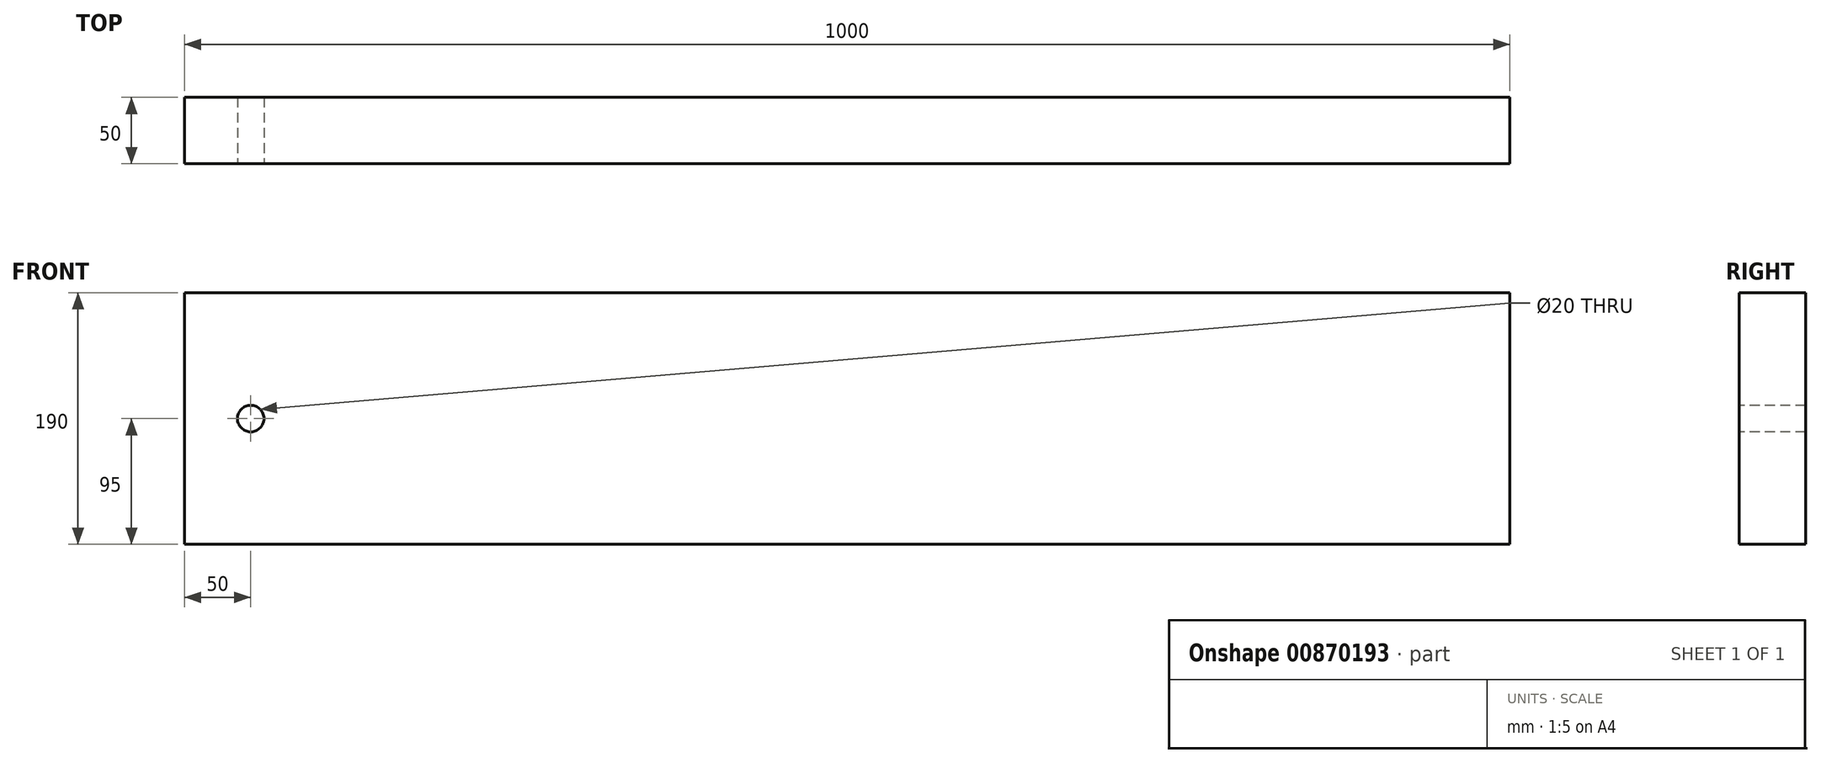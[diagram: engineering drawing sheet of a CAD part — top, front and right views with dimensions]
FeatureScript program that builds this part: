
annotation { "Feature Type Name" : "Feature", "Feature Type Description" : "" }
export const myFeature = defineFeature(function(context is Context, id is Id, definition is map)
    precondition{}
    {
        {
            var Q0;
            Q0=qCreatedBy(makeId("Right.planeOp"),FACE);
            var sketch = newSketch(context, id + "F0", { "sketchPlane" : qUnion([Q0])});
            skLineSegment(sketch, "E0.bottom", {"start": v(25, -95) * mm, "end": v(-25, -95) * mm});
            skLineSegment(sketch, "E0.top", {"start": v(25, 95) * mm, "end": v(-25, 95) * mm});
            skLineSegment(sketch, "E0.left", {"start": v(25, -95) * mm, "end": v(25, 95) * mm});
            skLineSegment(sketch, "E0.right", {"start": v(-25, -95) * mm, "end": v(-25, 95) * mm});
            skPoint(sketch, "E0.middle", {"position": v(0, 0) * mm});
            skSolve(sketch);
        }
        {
            var Q0;
            Q0 = qSketchRegion(id + "F0", true);
            extrude(context, id + "F1", {"entities" : qUnion([Q0]), "endBound" : BoundingType.SYMMETRIC, "depth" : 1000 * mm, "offsetDistance" : 25 * mm});
        }
        {
            var Q0;
            Q0=makeQuery(id+"F1.opExtrude","SWEPT_FACE",FACE,{"disambiguationData":[OSD([sQuery(id+"F0.wireOp",EDGE,"E0.right")])]});
            var sketch = newSketch(context, id + "F2", { "sketchPlane" : qUnion([Q0])});
            skSolve(sketch);
        }
        {
            var Q0;
            {var subQ0=sQuery(id+"F0.wireOp",EDGE,"E0.right");Q0=makeQuery(id+"F2.imprint","IMPRINT",FACE,{"disambiguationData":[TD([[makeQuery(id+"F2.imprint","IMPRINT",EDGE,{"derivedFrom":makeQuery(id+"F1.opExtrude","CAP_EDGE",EDGE,{"disambiguationData":[OSD([subQ0])],"isStart":true})}),-1.0]])]});}
            var sketch = newSketch(context, id + "F3", { "sketchPlane" : qUnion([Q0])});
            skCircle(sketch, "E1", {"center": v(-450, 0) * mm, "radius": 10 * mm});
            skSolve(sketch);
        }
        {
            var Q0;
            Q0=makeQuery(id+"F3.imprint","IMPRINT",FACE,{"disambiguationData":[TD([[makeQuery(id+"F3.imprint","IMPRINT",EDGE,{"derivedFrom":sQuery(id+"F3.wireOp",EDGE,"E1")}),1.0]])]});
            extrude(context, id + "F4", {"entities" : qUnion([Q0]), "operationType" : NewBodyOperationType.REMOVE, "endBound" : BoundingType.THROUGH_ALL, "oppositeDirection" : true, "depth" : 25 * mm, "offsetDistance" : 25 * mm});
        }
    });
